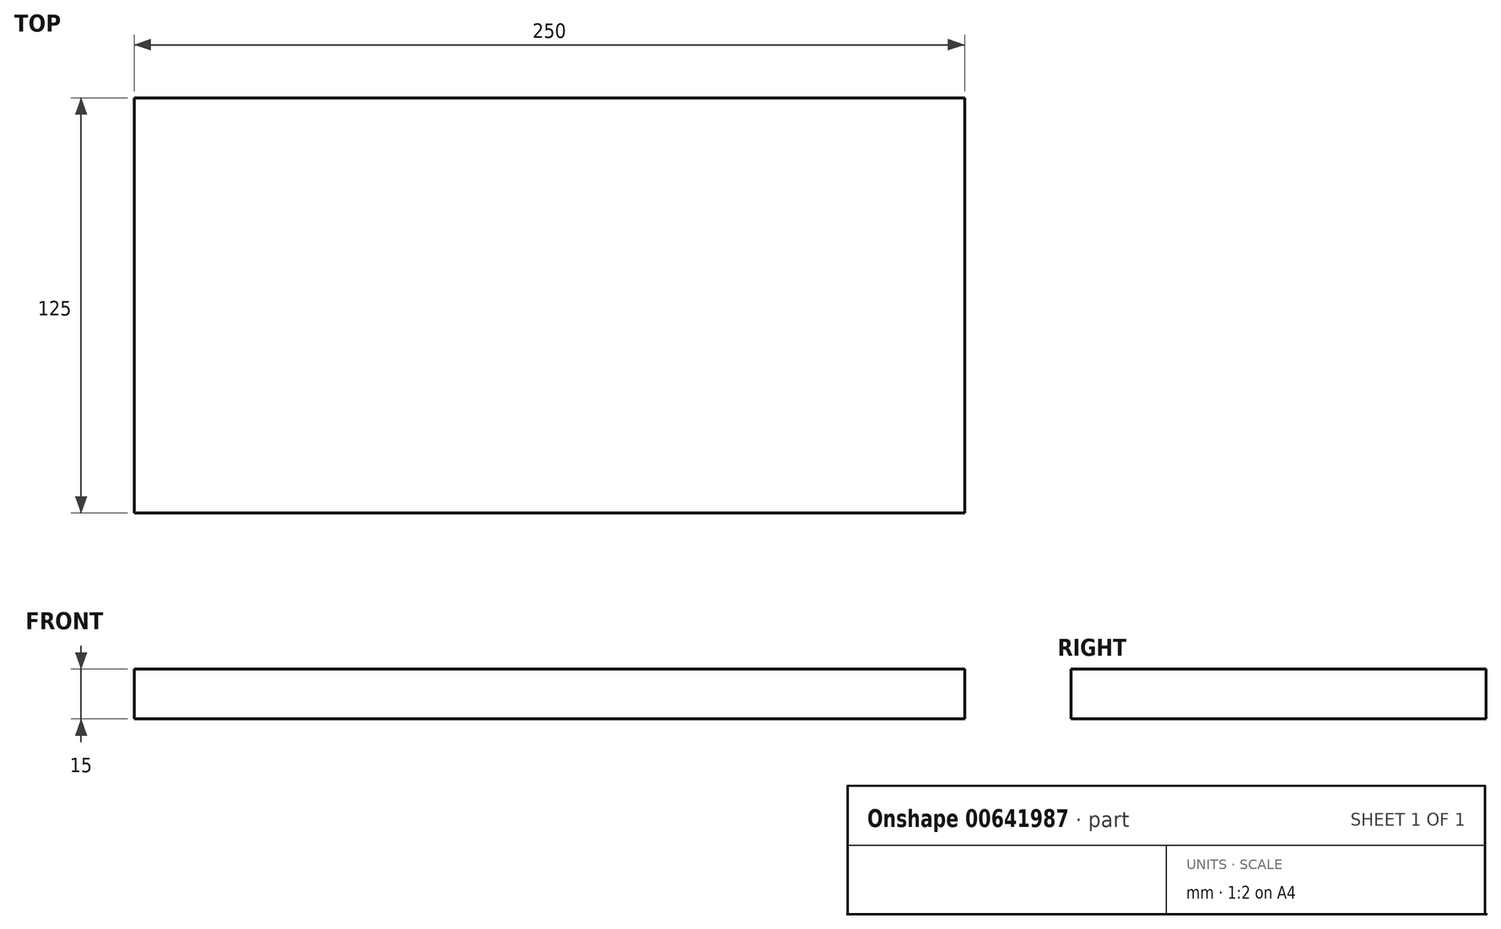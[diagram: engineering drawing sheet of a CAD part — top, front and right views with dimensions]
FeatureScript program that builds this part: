
annotation { "Feature Type Name" : "Feature", "Feature Type Description" : "" }
export const myFeature = defineFeature(function(context is Context, id is Id, definition is map)
    precondition{}
    {
        {
            var Q0;
            Q0=qCreatedBy(makeId("Top.planeOp"),FACE);
            var sketch = newSketch(context, id + "F0", { "sketchPlane" : qUnion([Q0])});
            skLineSegment(sketch, "E0.bottom", {"start": v(-125, 62.5) * mm, "end": v(125, 62.5) * mm});
            skLineSegment(sketch, "E0.top", {"start": v(-125, -62.5) * mm, "end": v(125, -62.5) * mm});
            skLineSegment(sketch, "E0.left", {"start": v(-125, 62.5) * mm, "end": v(-125, -62.5) * mm});
            skLineSegment(sketch, "E0.right", {"start": v(125, 62.5) * mm, "end": v(125, -62.5) * mm});
            skLineSegment(sketch, "E1", {"start": v(-125, 62.5) * mm, "end": v(125, -62.5) * mm, "construction": true});
            skSolve(sketch);
        }
        {
            var Q0;
            Q0 = qSketchRegion(id + "F0", true);
            extrude(context, id + "F1", {"entities" : qUnion([Q0]), "depth" : 15 * mm, "offsetDistance" : 25 * mm});
        }
    });
